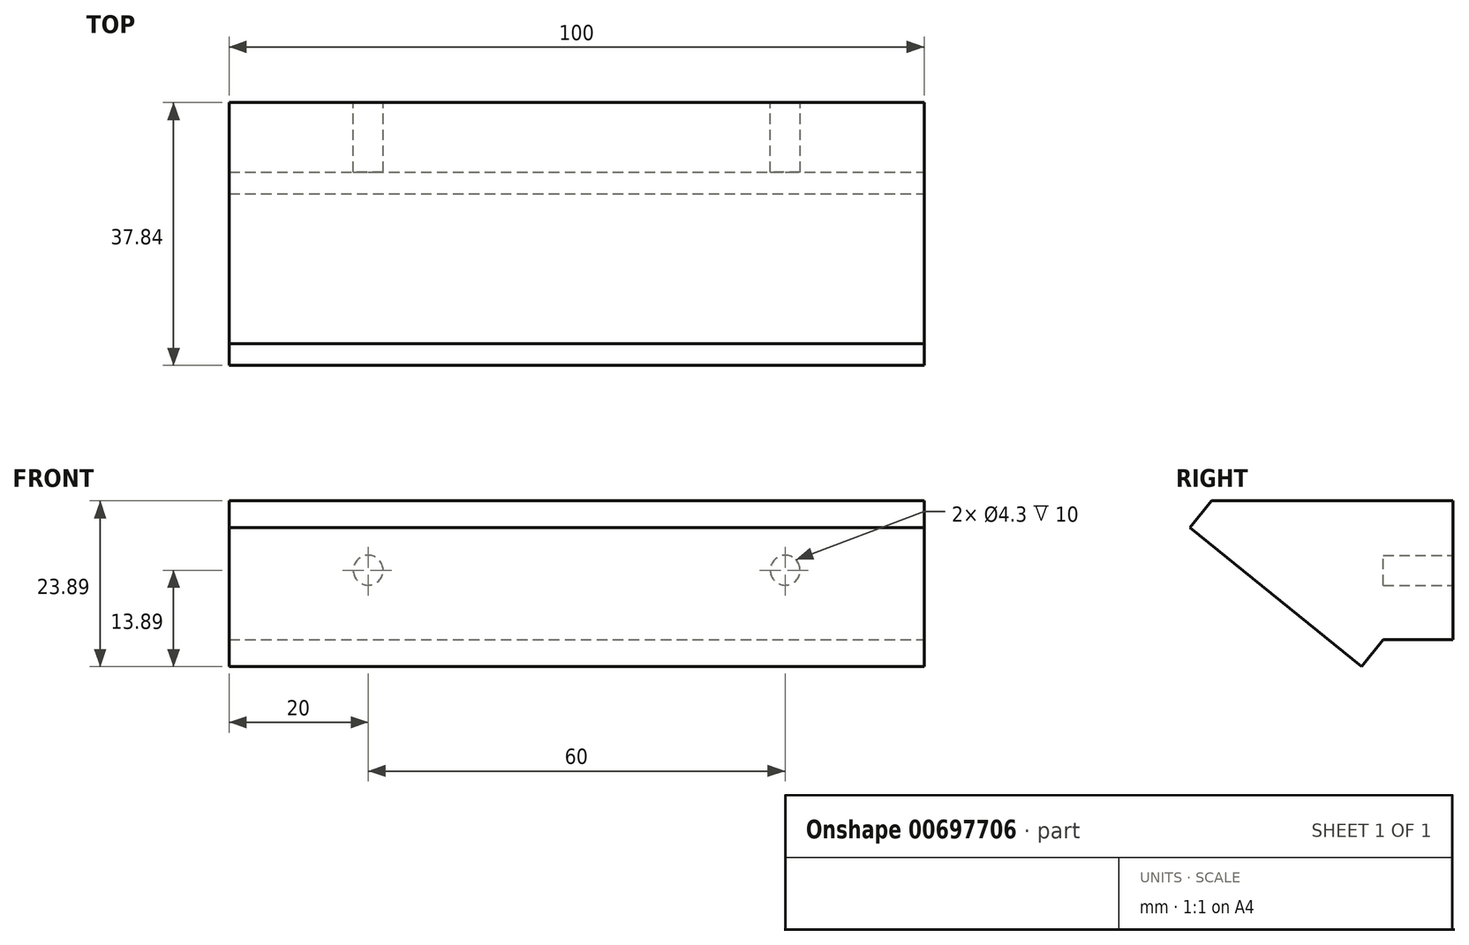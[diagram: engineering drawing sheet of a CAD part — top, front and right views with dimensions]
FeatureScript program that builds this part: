
annotation { "Feature Type Name" : "Feature", "Feature Type Description" : "" }
export const myFeature = defineFeature(function(context is Context, id is Id, definition is map)
    precondition{}
    {
        {
            var Q0;
            Q0=qCreatedBy(makeId("Front.planeOp"),FACE);
            var sketch = newSketch(context, id + "F0", { "sketchPlane" : qUnion([Q0])});
            skLineSegment(sketch, "E0.bottom", {"start": v(0, 0) * mm, "end": v(100, 0) * mm});
            skLineSegment(sketch, "E0.top", {"start": v(0, 20) * mm, "end": v(100, 20) * mm});
            skLineSegment(sketch, "E0.left", {"start": v(0, 0) * mm, "end": v(0, 20) * mm});
            skLineSegment(sketch, "E0.right", {"start": v(100, 0) * mm, "end": v(100, 20) * mm});
            skLineSegment(sketch, "E1", {"start": v(0, 10) * mm, "end": v(100, 10) * mm});
            skLineSegment(sketch, "E2", {"start": v(50, 20) * mm, "end": v(50, 0) * mm});
            skCircle(sketch, "E3", {"center": v(20, 10) * mm, "radius": 2.15 * mm});
            skCircle(sketch, "E4.MirrorC", {"center": v(80, 10) * mm, "radius": 2.15 * mm});
            skSolve(sketch);
        }
        {
            var Q0;
            {var subQ1=sQuery(id+"F0.wireOp",EDGE,"E0.left");var subQ8=sQuery(id+"F0.wireOp",EDGE,"E0.top");var subQ9=makeQuery(id+"F0.imprint","INTERSECT",VERTEX,{"derivedFrom":[subQ8,subQ1]});Q0=makeQuery(id+"F0.imprint","IMPRINT",FACE,{"disambiguationData":[TD([[makeQuery(id+"F0.imprint","IMPRINT",EDGE,{"disambiguationData":[TD([[subQ9,-1.0]])],"derivedFrom":subQ8}),-1.0]])]});}
            var Q1;
            {var subQ5=sQuery(id+"F0.wireOp",EDGE,"E0.right");var subQ6=sQuery(id+"F0.wireOp",EDGE,"E0.top");var subQ7=makeQuery(id+"F0.imprint","INTERSECT",VERTEX,{"derivedFrom":[subQ6,subQ5]});Q1=makeQuery(id+"F0.imprint","IMPRINT",FACE,{"disambiguationData":[TD([[makeQuery(id+"F0.imprint","IMPRINT",EDGE,{"disambiguationData":[TD([[subQ7,1.0]])],"derivedFrom":subQ6}),-1.0]])]});}
            var Q2;
            {var subQ1=sQuery(id+"F0.wireOp",EDGE,"E0.right");var subQ8=sQuery(id+"F0.wireOp",EDGE,"E0.bottom");var subQ9=makeQuery(id+"F0.imprint","INTERSECT",VERTEX,{"derivedFrom":[subQ8,subQ1]});Q2=makeQuery(id+"F0.imprint","IMPRINT",FACE,{"disambiguationData":[TD([[makeQuery(id+"F0.imprint","IMPRINT",EDGE,{"disambiguationData":[TD([[subQ9,1.0]])],"derivedFrom":subQ8}),1.0]])]});}
            var Q3;
            {var subQ1=sQuery(id+"F0.wireOp",EDGE,"E0.left");var subQ5=sQuery(id+"F0.wireOp",EDGE,"E0.bottom");var subQ6=makeQuery(id+"F0.imprint","INTERSECT",VERTEX,{"derivedFrom":[subQ5,subQ1]});Q3=makeQuery(id+"F0.imprint","IMPRINT",FACE,{"disambiguationData":[TD([[makeQuery(id+"F0.imprint","IMPRINT",EDGE,{"disambiguationData":[TD([[subQ6,-1.0]])],"derivedFrom":subQ5}),1.0]])]});}
            extrude(context, id + "F1", {"entities" : qUnion([Q0, Q1, Q2, Q3]), "depth" : 10 * mm, "offsetDistance" : 25 * mm});
        }
        {
            var Q0;
            Q0=makeQuery(id+"F1.opExtrude","SWEPT_FACE",FACE,{"disambiguationData":[OSD([sQuery(id+"F0.wireOp",EDGE,"E0.right")])]});
            var sketch = newSketch(context, id + "F2", { "sketchPlane" : qUnion([Q0])});
            skLineSegment(sketch, "E5.0.0", {"start": v(0, 0) * mm, "end": v(0, 20) * mm});
            skLineSegment(sketch, "E5.0.1", {"start": v(0, 20) * mm, "end": v(-10, 20) * mm});
            skLineSegment(sketch, "E5.0.2", {"start": v(-10, 20) * mm, "end": v(-10, 0) * mm});
            skLineSegment(sketch, "E5.0.3", {"start": v(-10, 0) * mm, "end": v(0, 0) * mm});
            skLineSegment(sketch, "E6", {"start": v(-10, 0) * mm, "end": v(-34.7, 20) * mm});
            skLineSegment(sketch, "E7", {"start": v(-10, 20) * mm, "end": v(-34.7, 20) * mm});
            skLineSegment(sketch, "E8", {"start": v(-34.7, 20) * mm, "end": v(-37.84, 16.11) * mm});
            skLineSegment(sketch, "E9", {"start": v(-37.84, 16.11) * mm, "end": v(-13.15, -3.89) * mm});
            skLineSegment(sketch, "E10", {"start": v(-13.15, -3.89) * mm, "end": v(-10, 0) * mm});
            skSolve(sketch);
        }
        {
            var Q0;
            Q0=makeQuery(id+"F2.imprint","IMPRINT",FACE,{"disambiguationData":[TD([[makeQuery(id+"F2.imprint","IMPRINT",EDGE,{"derivedFrom":sQuery(id+"F2.wireOp",EDGE,"E5.0.2")}),1.0]])]});
            var Q1;
            Q1=makeQuery(id+"F2.imprint","IMPRINT",FACE,{"disambiguationData":[TD([[makeQuery(id+"F2.imprint","IMPRINT",EDGE,{"derivedFrom":sQuery(id+"F2.wireOp",EDGE,"E6")}),1.0]])]});
            var Q2;
            Q2=makeQuery(id+"F1.opExtrude","SWEPT_FACE",FACE,{"disambiguationData":[OSD([sQuery(id+"F0.wireOp",EDGE,"E0.left")])]});
            extrude(context, id + "F3", {"entities" : qUnion([Q0, Q1]), "operationType" : NewBodyOperationType.ADD, "endBound" : BoundingType.UP_TO_SURFACE, "oppositeDirection" : true, "depth" : 25 * mm, "endBoundEntityFace" : qUnion([Q2]), "offsetDistance" : 25 * mm});
        }
    });
